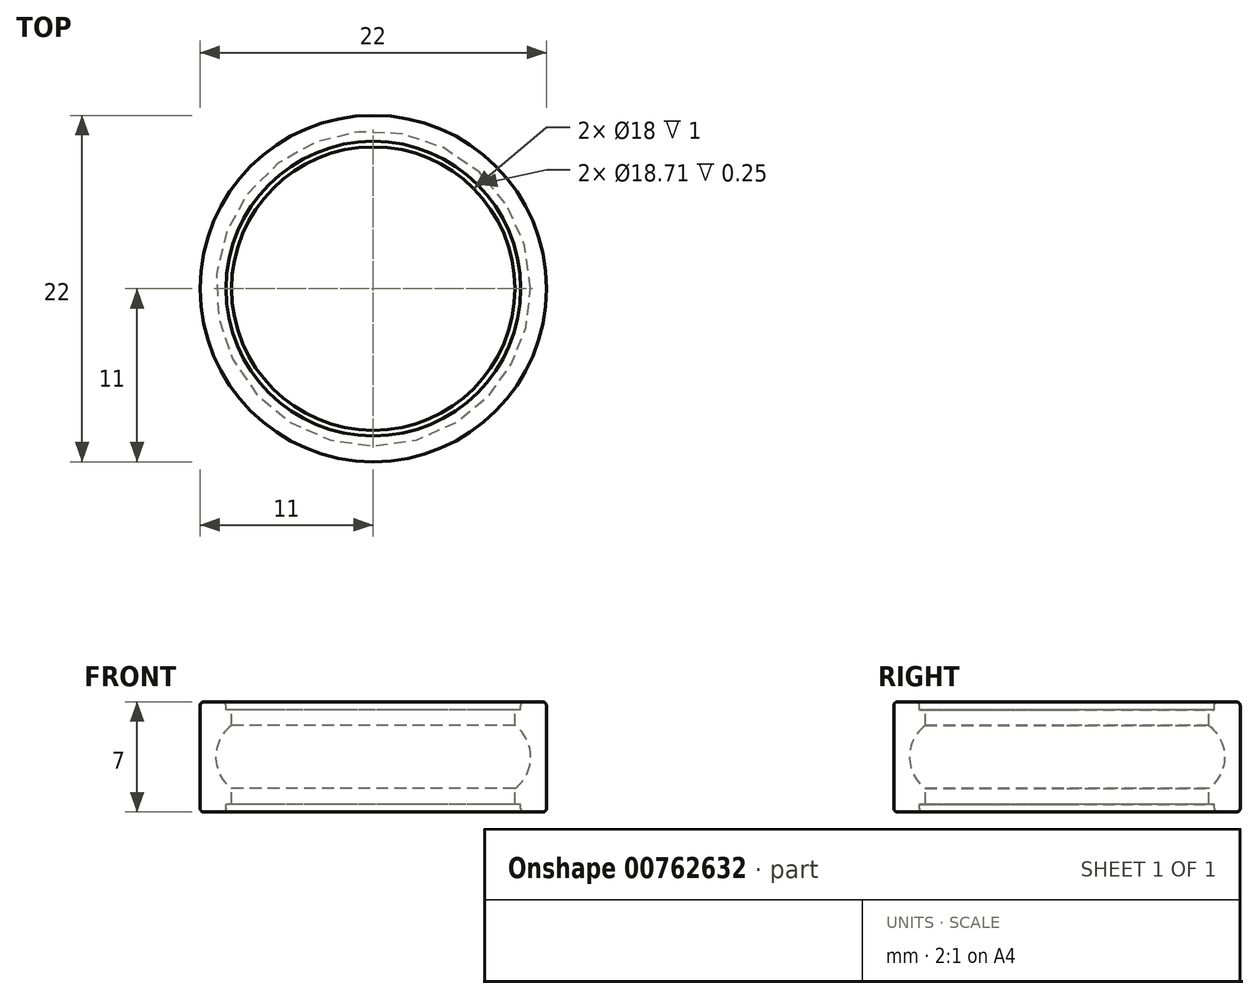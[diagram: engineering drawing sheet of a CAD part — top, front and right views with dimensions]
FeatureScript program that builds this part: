
annotation { "Feature Type Name" : "Feature", "Feature Type Description" : "" }
export const myFeature = defineFeature(function(context is Context, id is Id, definition is map)
    precondition{}
    {
        {
            var Q0;
            Q0=qCreatedBy(makeId("Front.planeOp"),FACE);
            var sketch = newSketch(context, id + "F0", { "sketchPlane" : qUnion([Q0])});
            skLineSegment(sketch, "E0", {"start": v(0, 2.1) * mm, "end": v(0, -2.2) * mm});
            skLineSegment(sketch, "E1", {"start": v(9, 0) * mm, "end": v(11, 0) * mm});
            skLineSegment(sketch, "E2", {"start": v(11, 0) * mm, "end": v(11, 3.25) * mm});
            skLineSegment(sketch, "E3", {"start": v(11, 0) * mm, "end": v(11, -3.25) * mm});
            skLineSegment(sketch, "E4", {"start": v(10.75, -3.5) * mm, "end": v(9.6, -3.5) * mm});
            skLineSegment(sketch, "E5", {"start": v(10.75, 3.5) * mm, "end": v(9.6, 3.5) * mm});
            skArc(sketch, "E6", {"start": v(9, -2) * mm, "mid": v(10, 0) * mm, "end": v(9, 2) * mm});
            skLineSegment(sketch, "E7", {"start": v(9, 3) * mm, "end": v(9, 2) * mm});
            skPoint(sketch, "E8.visualSharp", {"position": v(11, 3.5) * mm});
            skArc(sketch, "E8.filletArc", {"start": v(11, 3.25) * mm, "mid": v(10.93, 3.43) * mm, "end": v(10.75, 3.5) * mm});
            skPoint(sketch, "E9.visualSharp", {"position": v(11, -3.5) * mm});
            skArc(sketch, "E9.filletArc", {"start": v(10.75, -3.5) * mm, "mid": v(10.93, -3.43) * mm, "end": v(11, -3.25) * mm});
            skPoint(sketch, "E10.visualSharp", {"position": v(9, -3.5) * mm});
            skPoint(sketch, "E11.visualSharp", {"position": v(9, 3.5) * mm});
            skPoint(sketch, "E12.end.orphan", {"position": v(4, 0) * mm});
            skLineSegment(sketch, "E13.trimOffspring", {"start": v(9, -2) * mm, "end": v(9, -3) * mm});
            skLineSegment(sketch, "E14", {"start": v(9.36, 3.25) * mm, "end": v(9.36, 3) * mm});
            skLineSegment(sketch, "E15", {"start": v(9, -3) * mm, "end": v(9.36, -3) * mm});
            skLineSegment(sketch, "E16", {"start": v(9, 3) * mm, "end": v(9.36, 3) * mm});
            skLineSegment(sketch, "E17.trimOffspring", {"start": v(9.36, -3) * mm, "end": v(9.36, -3.25) * mm});
            skPoint(sketch, "E18.visualSharp", {"position": v(9.36, 3.5) * mm});
            skArc(sketch, "E18.filletArc", {"start": v(9.6, 3.5) * mm, "mid": v(9.43, 3.43) * mm, "end": v(9.36, 3.25) * mm});
            skPoint(sketch, "E19.visualSharp", {"position": v(9.36, -3.5) * mm});
            skArc(sketch, "E19.filletArc", {"start": v(9.36, -3.25) * mm, "mid": v(9.43, -3.43) * mm, "end": v(9.6, -3.5) * mm});
            skSolve(sketch);
        }
        {
            var Q0;
            Q0=qSketchRegion(id+"F0",true);
            var Q1;
            Q1=sQuery(id+"F0.wireOp",EDGE,"E0");
            revolve(context, id + "F1", {"surfaceOperationType" : NewSurfaceOperationType.NEW, "entities" : qUnion([Q0]), "axis" : qUnion([Q1]), "revolveType" : RevolveType.FULL});
        }
    });
